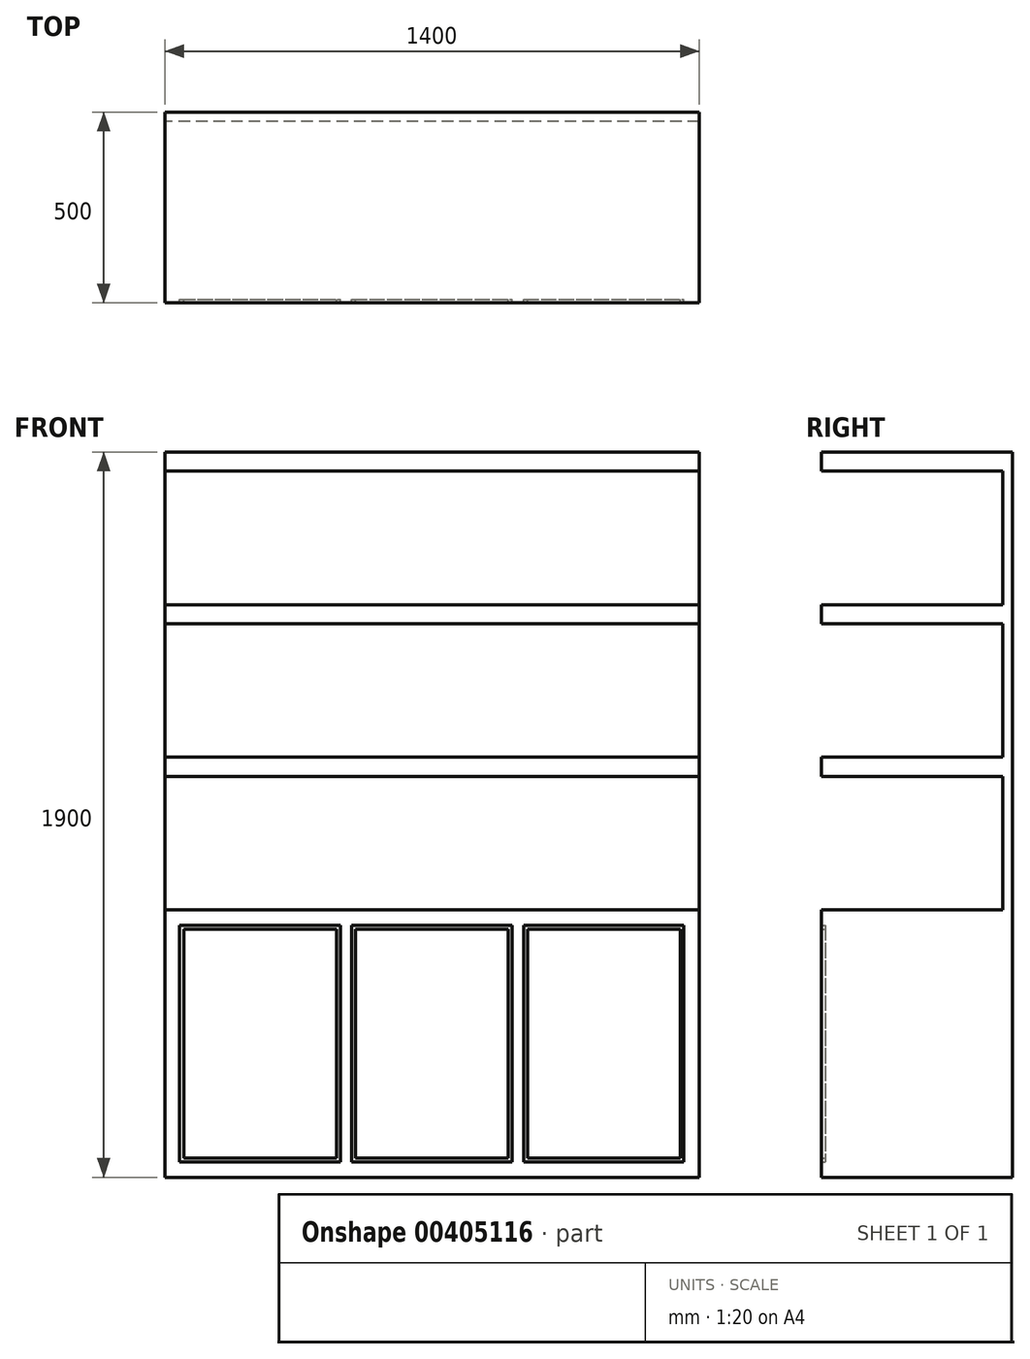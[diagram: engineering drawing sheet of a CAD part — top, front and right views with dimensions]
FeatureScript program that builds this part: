
annotation { "Feature Type Name" : "Feature", "Feature Type Description" : "" }
export const myFeature = defineFeature(function(context is Context, id is Id, definition is map)
    precondition{}
    {
        {
            var Q0;
            Q0=qCreatedBy(makeId("Front.planeOp"),FACE);
            var sketch = newSketch(context, id + "F0", { "sketchPlane" : qUnion([Q0])});
            skLineSegment(sketch, "E0.bottom", {"start": v(-700, 0) * mm, "end": v(700, 0) * mm});
            skLineSegment(sketch, "E0.top", {"start": v(-700, 700) * mm, "end": v(700, 700) * mm});
            skLineSegment(sketch, "E0.left", {"start": v(-700, 0) * mm, "end": v(-700, 700) * mm});
            skLineSegment(sketch, "E0.right", {"start": v(700, 0) * mm, "end": v(700, 700) * mm});
            skLineSegment(sketch, "E1.bottom", {"start": v(-650, 650) * mm, "end": v(-250, 650) * mm});
            skLineSegment(sketch, "E1.top", {"start": v(-650, 50) * mm, "end": v(-250, 50) * mm});
            skLineSegment(sketch, "E1.left", {"start": v(-650, 650) * mm, "end": v(-650, 50) * mm});
            skLineSegment(sketch, "E1.right", {"start": v(-250, 650) * mm, "end": v(-250, 50) * mm});
            skLineSegment(sketch, "E2.bottom", {"start": v(-200, 650) * mm, "end": v(200, 650) * mm});
            skLineSegment(sketch, "E2.top", {"start": v(-200, 50) * mm, "end": v(200, 50) * mm});
            skLineSegment(sketch, "E2.left", {"start": v(-200, 650) * mm, "end": v(-200, 50) * mm});
            skLineSegment(sketch, "E2.right", {"start": v(200, 650) * mm, "end": v(200, 50) * mm});
            skLineSegment(sketch, "E3.bottom", {"start": v(250, 650) * mm, "end": v(650, 650) * mm});
            skLineSegment(sketch, "E3.top", {"start": v(250, 50) * mm, "end": v(650, 50) * mm});
            skLineSegment(sketch, "E3.left", {"start": v(250, 650) * mm, "end": v(250, 50) * mm});
            skLineSegment(sketch, "E3.right", {"start": v(650, 650) * mm, "end": v(650, 50) * mm});
            skLineSegment(sketch, "E4.bottom", {"start": v(-700, 1050) * mm, "end": v(700, 1050) * mm});
            skLineSegment(sketch, "E4.top", {"start": v(-700, 1100) * mm, "end": v(700, 1100) * mm});
            skLineSegment(sketch, "E4.left", {"start": v(-700, 1050) * mm, "end": v(-700, 1100) * mm});
            skLineSegment(sketch, "E4.right", {"start": v(700, 1050) * mm, "end": v(700, 1100) * mm});
            skLineSegment(sketch, "E5.bottom", {"start": v(-700, 1450) * mm, "end": v(700, 1450) * mm});
            skLineSegment(sketch, "E5.top", {"start": v(-700, 1500) * mm, "end": v(700, 1500) * mm});
            skLineSegment(sketch, "E5.left", {"start": v(-700, 1450) * mm, "end": v(-700, 1500) * mm});
            skLineSegment(sketch, "E5.right", {"start": v(700, 1450) * mm, "end": v(700, 1500) * mm});
            skLineSegment(sketch, "E6.bottom", {"start": v(-700, 1850) * mm, "end": v(700, 1850) * mm});
            skLineSegment(sketch, "E6.top", {"start": v(-700, 1900) * mm, "end": v(700, 1900) * mm});
            skLineSegment(sketch, "E6.left", {"start": v(-700, 1850) * mm, "end": v(-700, 1900) * mm});
            skLineSegment(sketch, "E6.right", {"start": v(700, 1850) * mm, "end": v(700, 1900) * mm});
            skLineSegment(sketch, "E7", {"start": v(-700, 1850) * mm, "end": v(-700, 1500) * mm});
            skLineSegment(sketch, "E8", {"start": v(-700, 1450) * mm, "end": v(-700, 1100) * mm});
            skLineSegment(sketch, "E9", {"start": v(-700, 1050) * mm, "end": v(-700, 700) * mm});
            skLineSegment(sketch, "E10", {"start": v(700, 1850) * mm, "end": v(700, 1500) * mm});
            skLineSegment(sketch, "E11", {"start": v(700, 1450) * mm, "end": v(700, 1100) * mm});
            skLineSegment(sketch, "E12", {"start": v(700, 1050) * mm, "end": v(700, 700) * mm});
            skLineSegment(sketch, "E13.bottom", {"start": v(-660.9, 660) * mm, "end": v(-240, 660) * mm});
            skLineSegment(sketch, "E13.top", {"start": v(-660.9, 40) * mm, "end": v(-240, 40) * mm});
            skLineSegment(sketch, "E13.left", {"start": v(-660.9, 660) * mm, "end": v(-660.9, 40) * mm});
            skLineSegment(sketch, "E13.right", {"start": v(-240, 660) * mm, "end": v(-240, 40) * mm});
            skLineSegment(sketch, "E14.bottom", {"start": v(-210, 660) * mm, "end": v(210, 660) * mm});
            skLineSegment(sketch, "E14.top", {"start": v(-210, 40) * mm, "end": v(210, 40) * mm});
            skLineSegment(sketch, "E14.left", {"start": v(-210, 660) * mm, "end": v(-210, 40) * mm});
            skLineSegment(sketch, "E14.right", {"start": v(210, 660) * mm, "end": v(210, 40) * mm});
            skLineSegment(sketch, "E15.bottom", {"start": v(240, 660) * mm, "end": v(660, 660) * mm});
            skLineSegment(sketch, "E15.top", {"start": v(240, 40) * mm, "end": v(660, 40) * mm});
            skLineSegment(sketch, "E15.left", {"start": v(240, 660) * mm, "end": v(240, 40) * mm});
            skLineSegment(sketch, "E15.right", {"start": v(660, 660) * mm, "end": v(660, 40) * mm});
            skSolve(sketch);
        }
        {
            var Q0;
            Q0=makeQuery(id+"F0.imprint","IMPRINT",FACE,{"disambiguationData":[TD([[makeQuery(id+"F0.imprint","IMPRINT",EDGE,{"derivedFrom":sQuery(id+"F0.wireOp",EDGE,"E0.bottom")}),1.0]])]});
            var Q1;
            Q1=makeQuery(id+"F0.imprint","IMPRINT",FACE,{"disambiguationData":[TD([[makeQuery(id+"F0.imprint","IMPRINT",EDGE,{"derivedFrom":sQuery(id+"F0.wireOp",EDGE,"E3.bottom")}),1.0]])]});
            var Q2;
            Q2=makeQuery(id+"F0.imprint","IMPRINT",FACE,{"disambiguationData":[TD([[makeQuery(id+"F0.imprint","IMPRINT",EDGE,{"derivedFrom":sQuery(id+"F0.wireOp",EDGE,"E3.bottom")}),-1.0]])]});
            var Q3;
            Q3=makeQuery(id+"F0.imprint","IMPRINT",FACE,{"disambiguationData":[TD([[makeQuery(id+"F0.imprint","IMPRINT",EDGE,{"derivedFrom":sQuery(id+"F0.wireOp",EDGE,"E2.bottom")}),-1.0]])]});
            var Q4;
            Q4=makeQuery(id+"F0.imprint","IMPRINT",FACE,{"disambiguationData":[TD([[makeQuery(id+"F0.imprint","IMPRINT",EDGE,{"derivedFrom":sQuery(id+"F0.wireOp",EDGE,"E2.bottom")}),1.0]])]});
            var Q5;
            Q5=makeQuery(id+"F0.imprint","IMPRINT",FACE,{"disambiguationData":[TD([[makeQuery(id+"F0.imprint","IMPRINT",EDGE,{"derivedFrom":sQuery(id+"F0.wireOp",EDGE,"E1.bottom")}),-1.0]])]});
            var Q6;
            Q6=makeQuery(id+"F0.imprint","IMPRINT",FACE,{"disambiguationData":[TD([[makeQuery(id+"F0.imprint","IMPRINT",EDGE,{"derivedFrom":sQuery(id+"F0.wireOp",EDGE,"E1.bottom")}),1.0]])]});
            var Q7;
            Q7=makeQuery(id+"F0.imprint","IMPRINT",FACE,{"disambiguationData":[TD([[makeQuery(id+"F0.imprint","IMPRINT",EDGE,{"derivedFrom":sQuery(id+"F0.wireOp",EDGE,"E0.top")}),1.0]])]});
            var Q8;
            Q8=makeQuery(id+"F0.imprint","IMPRINT",FACE,{"disambiguationData":[TD([[makeQuery(id+"F0.imprint","IMPRINT",EDGE,{"derivedFrom":sQuery(id+"F0.wireOp",EDGE,"E4.bottom")}),1.0]])]});
            var Q9;
            Q9=makeQuery(id+"F0.imprint","IMPRINT",FACE,{"disambiguationData":[TD([[makeQuery(id+"F0.imprint","IMPRINT",EDGE,{"derivedFrom":sQuery(id+"F0.wireOp",EDGE,"E4.top")}),1.0]])]});
            var Q10;
            Q10=makeQuery(id+"F0.imprint","IMPRINT",FACE,{"disambiguationData":[TD([[makeQuery(id+"F0.imprint","IMPRINT",EDGE,{"derivedFrom":sQuery(id+"F0.wireOp",EDGE,"E5.bottom")}),1.0]])]});
            var Q11;
            Q11=makeQuery(id+"F0.imprint","IMPRINT",FACE,{"disambiguationData":[TD([[makeQuery(id+"F0.imprint","IMPRINT",EDGE,{"derivedFrom":sQuery(id+"F0.wireOp",EDGE,"E5.top")}),1.0]])]});
            var Q12;
            Q12=makeQuery(id+"F0.imprint","IMPRINT",FACE,{"disambiguationData":[TD([[makeQuery(id+"F0.imprint","IMPRINT",EDGE,{"derivedFrom":sQuery(id+"F0.wireOp",EDGE,"E6.bottom")}),1.0]])]});
            extrude(context, id + "F1", {"entities" : qUnion([Q0, Q1, Q2, Q3, Q4, Q5, Q6, Q7, Q8, Q9, Q10, Q11, Q12]), "depth" : 25 * mm});
        }
        {
            var Q0;
            Q0=makeQuery(id+"F0.imprint","IMPRINT",FACE,{"disambiguationData":[TD([[makeQuery(id+"F0.imprint","IMPRINT",EDGE,{"derivedFrom":sQuery(id+"F0.wireOp",EDGE,"E6.bottom")}),1.0]])]});
            var Q1;
            Q1=makeQuery(id+"F0.imprint","IMPRINT",FACE,{"disambiguationData":[TD([[makeQuery(id+"F0.imprint","IMPRINT",EDGE,{"derivedFrom":sQuery(id+"F0.wireOp",EDGE,"E5.bottom")}),1.0]])]});
            var Q2;
            Q2=makeQuery(id+"F0.imprint","IMPRINT",FACE,{"disambiguationData":[TD([[makeQuery(id+"F0.imprint","IMPRINT",EDGE,{"derivedFrom":sQuery(id+"F0.wireOp",EDGE,"E4.bottom")}),1.0]])]});
            var Q3;
            Q3=makeQuery(id+"F0.imprint","IMPRINT",FACE,{"disambiguationData":[TD([[makeQuery(id+"F0.imprint","IMPRINT",EDGE,{"derivedFrom":sQuery(id+"F0.wireOp",EDGE,"E0.bottom")}),1.0]])]});
            var Q4;
            Q4=makeQuery(id+"F0.imprint","IMPRINT",FACE,{"disambiguationData":[TD([[makeQuery(id+"F0.imprint","IMPRINT",EDGE,{"derivedFrom":sQuery(id+"F0.wireOp",EDGE,"E1.bottom")}),-1.0]])]});
            var Q5;
            Q5=makeQuery(id+"F0.imprint","IMPRINT",FACE,{"disambiguationData":[TD([[makeQuery(id+"F0.imprint","IMPRINT",EDGE,{"derivedFrom":sQuery(id+"F0.wireOp",EDGE,"E2.bottom")}),-1.0]])]});
            var Q6;
            Q6=makeQuery(id+"F0.imprint","IMPRINT",FACE,{"disambiguationData":[TD([[makeQuery(id+"F0.imprint","IMPRINT",EDGE,{"derivedFrom":sQuery(id+"F0.wireOp",EDGE,"E3.bottom")}),-1.0]])]});
            var Q7;
            Q7=makeQuery(id+"F0.imprint","IMPRINT",FACE,{"disambiguationData":[TD([[makeQuery(id+"F0.imprint","IMPRINT",EDGE,{"derivedFrom":sQuery(id+"F0.wireOp",EDGE,"E3.bottom")}),1.0]])]});
            var Q8;
            Q8=makeQuery(id+"F0.imprint","IMPRINT",FACE,{"disambiguationData":[TD([[makeQuery(id+"F0.imprint","IMPRINT",EDGE,{"derivedFrom":sQuery(id+"F0.wireOp",EDGE,"E2.bottom")}),1.0]])]});
            var Q9;
            Q9=makeQuery(id+"F0.imprint","IMPRINT",FACE,{"disambiguationData":[TD([[makeQuery(id+"F0.imprint","IMPRINT",EDGE,{"derivedFrom":sQuery(id+"F0.wireOp",EDGE,"E1.bottom")}),1.0]])]});
            extrude(context, id + "F2", {"entities" : qUnion([Q0, Q1, Q2, Q3, Q4, Q5, Q6, Q7, Q8, Q9]), "operationType" : NewBodyOperationType.ADD, "depth" : 500 * mm});
        }
        {
            var Q0;
            Q0=makeQuery(id+"F0.imprint","IMPRINT",FACE,{"disambiguationData":[TD([[makeQuery(id+"F0.imprint","IMPRINT",EDGE,{"derivedFrom":sQuery(id+"F0.wireOp",EDGE,"E3.bottom")}),1.0]])]});
            var Q1;
            Q1=makeQuery(id+"F0.imprint","IMPRINT",FACE,{"disambiguationData":[TD([[makeQuery(id+"F0.imprint","IMPRINT",EDGE,{"derivedFrom":sQuery(id+"F0.wireOp",EDGE,"E2.bottom")}),1.0]])]});
            var Q2;
            Q2=makeQuery(id+"F0.imprint","IMPRINT",FACE,{"disambiguationData":[TD([[makeQuery(id+"F0.imprint","IMPRINT",EDGE,{"derivedFrom":sQuery(id+"F0.wireOp",EDGE,"E1.bottom")}),1.0]])]});
            var Q3;
            Q3=makeQuery(id+"F2.opExtrude","CAP_FACE",FACE,{"disambiguationData":[OSD([sQuery(id+"F0.wireOp",EDGE,"E0.bottom"),sQuery(id+"F0.wireOp",EDGE,"E0.top"),sQuery(id+"F0.wireOp",EDGE,"E0.left"),sQuery(id+"F0.wireOp",EDGE,"E0.right")])],"isStart":false});
            extrude(context, id + "F3", {"entities" : qUnion([Q0, Q1, Q2]), "operationType" : NewBodyOperationType.REMOVE, "endBound" : BoundingType.UP_TO_SURFACE, "endBoundEntityFace" : qUnion([Q3]), "depth" : 25 * mm, "hasSecondDirection" : true, "secondDirectionOppositeDirection" : false, "secondDirectionDepth" : 490 * mm});
        }
    });
